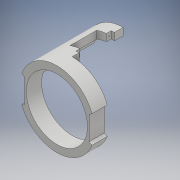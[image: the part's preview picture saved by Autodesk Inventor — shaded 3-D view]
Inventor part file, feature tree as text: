
AUTODESK INVENTOR PART (.ipt)
format: ipt  version: 2017 (Build 210142000, 142)  size: 168,448 bytes
history: native  units: mm
features: extrude x6, sketch x6, other x2, hole x2, plane x1
ambient origin geometry x8: Origin, YZ Plane, XZ Plane, XY Plane, X Axis, Y Axis, Z Axis, Center Point
bodies: Solid1 (feature_tree)
feature tree (17):
  extrude  "Extrusion1"  Depth=15.0mm TaperAngle=0.0deg
  extrude  "Extrusion2"  Depth=15.0mm TaperAngle=0.0deg
  extrude  "Extrusion3"  Depth=10.0mm TaperAngle=0.0deg
  extrude  "Extrusion4"  [1 undecoded]
  extrude  "Extrusion5"  [1 undecoded]
  plane  "Work Plane1"
  extrude  "Extrusion6"  [1 undecoded]
  other  "Work Point1"
  hole  "Hole1"  [1 undecoded]
  other  "Work Point2"
  hole  "Hole2"  [1 undecoded]
  sketch  "Sketch1"  dims[d0=15.0mm d1=0.0mm d2=15.0mm d3=0.0mm]
  sketch  "Sketch2"  dims[d4=15.0mm d5=0.0mm d6=15.0mm d7=0.0mm]
  sketch  "Sketch3"  dims[d8=50.0mm d9=0.0mm d10=10.0mm d11=0.0mm]
  sketch  "Sketch4"  dims[d12=10.0mm d13=10.0mm d14=1.0mm d15=6.0mm d16=3.023mm d17=2.0mm d18=14.3117mm d19=3.0mm d20=20.594885mm]
  sketch  "Sketch5"  dims[d21=10.0mm d22=10.0mm d23=1.0mm d24=6.0mm d25=3.023mm d26=2.0mm d27=14.3117mm d28=3.0mm d29=20.594885mm]
  sketch  "Sketch6"
note: 5 required parameter values undecoded (feature->parameter linkage not recoverable at this tier; creation-order binding heuristic only, values carry confidence <= 0.55)
